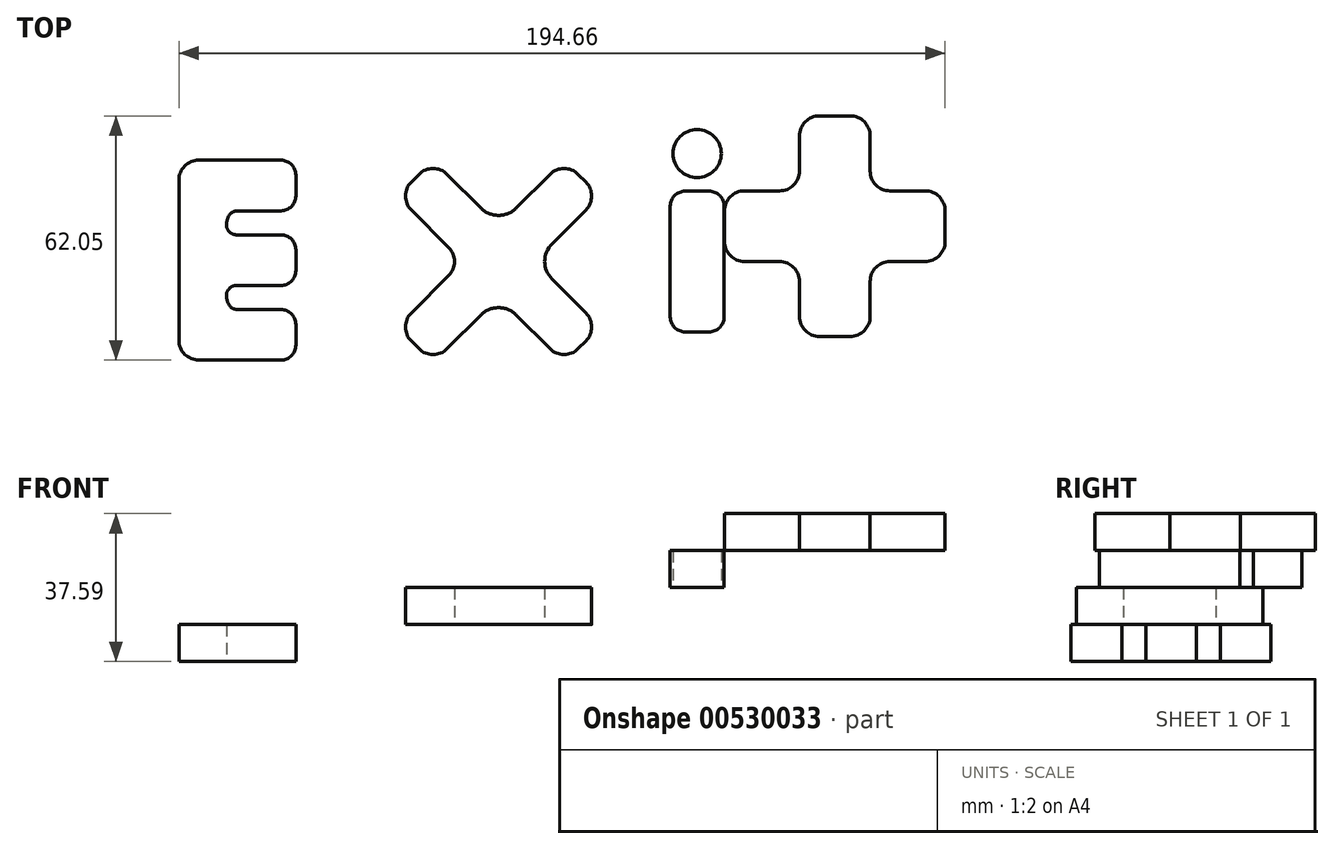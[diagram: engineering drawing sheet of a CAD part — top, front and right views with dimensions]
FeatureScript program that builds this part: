
annotation { "Feature Type Name" : "Feature", "Feature Type Description" : "" }
export const myFeature = defineFeature(function(context is Context, id is Id, definition is map)
    precondition{}
    {
        {
            var Q0;
            Q0=qCreatedBy(makeId("Top.planeOp"),FACE);
            var sketch = newSketch(context, id + "F0", { "sketchPlane" : qUnion([Q0])});
            skLineSegment(sketch, "E0", {"start": v(-56.56, 0.34) * mm, "end": v(-56.56, 20.66) * mm});
            skLineSegment(sketch, "E1", {"start": v(-56.56, 0.34) * mm, "end": v(-56.56, -19.98) * mm});
            skLineSegment(sketch, "E2", {"start": v(-51.48, 25.74) * mm, "end": v(-30.66, 25.74) * mm});
            skLineSegment(sketch, "E3", {"start": v(-26.85, 21.93) * mm, "end": v(-26.85, 16.69) * mm});
            skLineSegment(sketch, "E4", {"start": v(-30.66, 12.88) * mm, "end": v(-41.7, 12.88) * mm});
            skLineSegment(sketch, "E5", {"start": v(-51.48, -25.06) * mm, "end": v(-30.66, -25.06) * mm});
            skLineSegment(sketch, "E6", {"start": v(-26.85, -21.25) * mm, "end": v(-26.85, -16) * mm});
            skLineSegment(sketch, "E7", {"start": v(-30.66, -12.2) * mm, "end": v(-41.7, -12.2) * mm});
            skLineSegment(sketch, "E8", {"start": v(-44.4, 9.9) * mm, "end": v(-44.16, 10.93) * mm});
            skLineSegment(sketch, "E9", {"start": v(-44.4, -9.22) * mm, "end": v(-44.16, -10.24) * mm});
            skLineSegment(sketch, "E10", {"start": v(-41.94, 6.78) * mm, "end": v(-30.66, 6.78) * mm});
            skLineSegment(sketch, "E11", {"start": v(-26.85, 2.97) * mm, "end": v(-26.85, -2.28) * mm});
            skPoint(sketch, "E12.visualSharp", {"position": v(-56.56, 25.74) * mm});
            skArc(sketch, "E12.filletArc", {"start": v(-51.48, 25.74) * mm, "mid": v(-55.07, 24.26) * mm, "end": v(-56.56, 20.66) * mm});
            skPoint(sketch, "E13.visualSharp", {"position": v(-26.85, 25.74) * mm});
            skArc(sketch, "E13.filletArc", {"start": v(-26.85, 21.93) * mm, "mid": v(-27.96, 24.63) * mm, "end": v(-30.66, 25.74) * mm});
            skPoint(sketch, "E14.visualSharp", {"position": v(-56.56, -25.06) * mm});
            skArc(sketch, "E14.filletArc", {"start": v(-56.56, -19.98) * mm, "mid": v(-55.07, -23.57) * mm, "end": v(-51.48, -25.06) * mm});
            skPoint(sketch, "E15.visualSharp", {"position": v(-26.85, -25.06) * mm});
            skArc(sketch, "E15.filletArc", {"start": v(-30.66, -25.06) * mm, "mid": v(-27.96, -23.94) * mm, "end": v(-26.85, -21.25) * mm});
            skPoint(sketch, "E16.visualSharp", {"position": v(-26.85, -12.2) * mm});
            skArc(sketch, "E16.filletArc", {"start": v(-26.85, -16) * mm, "mid": v(-27.96, -13.3) * mm, "end": v(-30.66, -12.2) * mm});
            skPoint(sketch, "E17.visualSharp", {"position": v(-26.85, 12.88) * mm});
            skArc(sketch, "E17.filletArc", {"start": v(-30.66, 12.88) * mm, "mid": v(-27.96, 14) * mm, "end": v(-26.85, 16.69) * mm});
            skLineSegment(sketch, "E18", {"start": v(-30.66, -6.09) * mm, "end": v(-41.94, -6.09) * mm});
            skPoint(sketch, "E19.visualSharp", {"position": v(-26.85, 6.78) * mm});
            skArc(sketch, "E19.filletArc", {"start": v(-26.85, 2.97) * mm, "mid": v(-27.96, 5.66) * mm, "end": v(-30.66, 6.78) * mm});
            skPoint(sketch, "E20.visualSharp", {"position": v(-26.85, -6.09) * mm});
            skArc(sketch, "E20.filletArc", {"start": v(-30.66, -6.09) * mm, "mid": v(-27.96, -4.97) * mm, "end": v(-26.85, -2.28) * mm});
            skPoint(sketch, "E21.visualSharp", {"position": v(-45.15, 6.78) * mm});
            skArc(sketch, "E21.filletArc", {"start": v(-44.4, 9.9) * mm, "mid": v(-43.93, 7.74) * mm, "end": v(-41.94, 6.78) * mm});
            skPoint(sketch, "E22.visualSharp", {"position": v(-43.7, 12.88) * mm});
            skArc(sketch, "E22.filletArc", {"start": v(-41.7, 12.88) * mm, "mid": v(-43.26, 12.33) * mm, "end": v(-44.16, 10.93) * mm});
            skPoint(sketch, "E23.visualSharp", {"position": v(-45.15, -6.09) * mm});
            skArc(sketch, "E23.filletArc", {"start": v(-41.94, -6.09) * mm, "mid": v(-43.93, -7.05) * mm, "end": v(-44.4, -9.22) * mm});
            skPoint(sketch, "E24.visualSharp", {"position": v(-43.7, -12.2) * mm});
            skArc(sketch, "E24.filletArc", {"start": v(-44.16, -10.24) * mm, "mid": v(-43.26, -11.65) * mm, "end": v(-41.7, -12.2) * mm});
            skLineSegment(sketch, "E25", {"start": v(-30.66, 25.74) * mm, "end": v(20.45, 25.74) * mm});
            skLineSegment(sketch, "E26", {"start": v(-30.66, -25.06) * mm, "end": v(17.75, -25.06) * mm});
            skSolve(sketch);
        }
        {
            var Q0;
            Q0=makeQuery(id+"F0.imprint","IMPRINT",FACE,{"disambiguationData":[TD([[makeQuery(id+"F0.imprint","IMPRINT",EDGE,{"derivedFrom":sQuery(id+"F0.wireOp",EDGE,"E0")}),-1.0]])]});
            extrude(context, id + "F1", {"entities" : qUnion([Q0]), "depth" : 9.4 * mm, "offsetDistance" : 25.4 * mm});
        }
        {
            var Q0;
            Q0=makeQuery(id+"F1.opExtrude","CAP_FACE",FACE,{"disambiguationData":[OSD([sQuery(id+"F0.wireOp",EDGE,"E0"),sQuery(id+"F0.wireOp",EDGE,"E1"),sQuery(id+"F0.wireOp",EDGE,"E2"),sQuery(id+"F0.wireOp",EDGE,"E3"),sQuery(id+"F0.wireOp",EDGE,"E4"),sQuery(id+"F0.wireOp",EDGE,"E5"),sQuery(id+"F0.wireOp",EDGE,"E6"),sQuery(id+"F0.wireOp",EDGE,"E7"),sQuery(id+"F0.wireOp",EDGE,"E8"),sQuery(id+"F0.wireOp",EDGE,"E9"),sQuery(id+"F0.wireOp",EDGE,"E10"),sQuery(id+"F0.wireOp",EDGE,"E11"),sQuery(id+"F0.wireOp",EDGE,"E12.filletArc"),sQuery(id+"F0.wireOp",EDGE,"E13.filletArc"),sQuery(id+"F0.wireOp",EDGE,"E14.filletArc"),sQuery(id+"F0.wireOp",EDGE,"E15.filletArc"),sQuery(id+"F0.wireOp",EDGE,"E16.filletArc"),sQuery(id+"F0.wireOp",EDGE,"E17.filletArc"),sQuery(id+"F0.wireOp",EDGE,"E18"),sQuery(id+"F0.wireOp",EDGE,"E19.filletArc"),sQuery(id+"F0.wireOp",EDGE,"E20.filletArc"),sQuery(id+"F0.wireOp",EDGE,"E21.filletArc"),sQuery(id+"F0.wireOp",EDGE,"E22.filletArc"),sQuery(id+"F0.wireOp",EDGE,"E23.filletArc"),sQuery(id+"F0.wireOp",EDGE,"E24.filletArc")])],"isStart":false});
            var sketch = newSketch(context, id + "F2", { "sketchPlane" : qUnion([Q0])});
            skPoint(sketch, "E27.endSnap0", {"position": v(-55.07, -23.57) * mm});
            skLineSegment(sketch, "E28", {"start": v(4.41, 22.15) * mm, "end": v(2.5, 20.24) * mm});
            skLineSegment(sketch, "E29", {"start": v(2.5, 13.06) * mm, "end": v(11.96, 3.6) * mm});
            skLineSegment(sketch, "E30", {"start": v(11.6, 22.15) * mm, "end": v(20.16, 13.59) * mm});
            skLineSegment(sketch, "E31.MirrorCS", {"start": v(37.7, 22.15) * mm, "end": v(29.14, 13.59) * mm});
            skLineSegment(sketch, "E32.MirrorCS", {"start": v(46.8, 13.06) * mm, "end": v(38.24, 4.5) * mm});
            skLineSegment(sketch, "E33.MirrorCS", {"start": v(44.9, 22.15) * mm, "end": v(46.8, 20.24) * mm});
            skLineSegment(sketch, "E34.MirrorCS", {"start": v(46.8, -13.06) * mm, "end": v(38.24, -4.5) * mm});
            skLineSegment(sketch, "E35.MirrorCS", {"start": v(44.9, -22.15) * mm, "end": v(46.8, -20.24) * mm});
            skLineSegment(sketch, "E36.MirrorCS", {"start": v(37.7, -22.15) * mm, "end": v(29.14, -13.59) * mm});
            skLineSegment(sketch, "E37.MirrorCS", {"start": v(11.6, -22.15) * mm, "end": v(20.16, -13.59) * mm});
            skLineSegment(sketch, "E38.MirrorCS", {"start": v(2.5, -13.06) * mm, "end": v(11.96, -3.6) * mm});
            skLineSegment(sketch, "E39.MirrorCS", {"start": v(4.41, -22.15) * mm, "end": v(2.5, -20.24) * mm});
            skPoint(sketch, "E40.visualSharp", {"position": v(-1.1, 16.65) * mm});
            skArc(sketch, "E40.filletArc", {"start": v(2.5, 20.24) * mm, "mid": v(1.01, 16.65) * mm, "end": v(2.5, 13.06) * mm});
            skPoint(sketch, "E41.visualSharp", {"position": v(8, 25.74) * mm});
            skArc(sketch, "E41.filletArc", {"start": v(11.6, 22.15) * mm, "mid": v(8, 23.64) * mm, "end": v(4.41, 22.15) * mm});
            skPoint(sketch, "E42.visualSharp", {"position": v(-1.1, -16.65) * mm});
            skArc(sketch, "E42.filletArc", {"start": v(2.5, -13.06) * mm, "mid": v(1.01, -16.65) * mm, "end": v(2.5, -20.24) * mm});
            skPoint(sketch, "E43.visualSharp", {"position": v(8, -25.74) * mm});
            skArc(sketch, "E43.filletArc", {"start": v(4.41, -22.15) * mm, "mid": v(8, -23.64) * mm, "end": v(11.6, -22.15) * mm});
            skPoint(sketch, "E44.visualSharp", {"position": v(41.3, -25.74) * mm});
            skArc(sketch, "E44.filletArc", {"start": v(37.7, -22.15) * mm, "mid": v(41.3, -23.64) * mm, "end": v(44.9, -22.15) * mm});
            skPoint(sketch, "E45.visualSharp", {"position": v(50.4, -16.65) * mm});
            skArc(sketch, "E45.filletArc", {"start": v(46.8, -20.24) * mm, "mid": v(48.3, -16.65) * mm, "end": v(46.8, -13.06) * mm});
            skPoint(sketch, "E46.visualSharp", {"position": v(50.4, 16.65) * mm});
            skArc(sketch, "E46.filletArc", {"start": v(46.8, 13.06) * mm, "mid": v(48.3, 16.65) * mm, "end": v(46.8, 20.24) * mm});
            skPoint(sketch, "E47.visualSharp", {"position": v(41.3, 25.74) * mm});
            skArc(sketch, "E47.filletArc", {"start": v(44.9, 22.15) * mm, "mid": v(41.3, 23.64) * mm, "end": v(37.7, 22.15) * mm});
            skPoint(sketch, "E48.visualSharp", {"position": v(15.56, 0) * mm});
            skArc(sketch, "E48.filletArc", {"start": v(11.96, -3.6) * mm, "mid": v(13.45, 0) * mm, "end": v(11.96, 3.6) * mm});
            skPoint(sketch, "E49.visualSharp", {"position": v(24.65, 9.1) * mm});
            skArc(sketch, "E49.filletArc", {"start": v(20.16, 13.59) * mm, "mid": v(24.65, 11.73) * mm, "end": v(29.14, 13.59) * mm});
            skPoint(sketch, "E50.visualSharp", {"position": v(33.75, 0) * mm});
            skArc(sketch, "E50.filletArc", {"start": v(38.24, 4.5) * mm, "mid": v(36.38, 0) * mm, "end": v(38.24, -4.5) * mm});
            skPoint(sketch, "E51.visualSharp", {"position": v(24.65, -9.1) * mm});
            skArc(sketch, "E51.filletArc", {"start": v(29.14, -13.59) * mm, "mid": v(24.65, -11.73) * mm, "end": v(20.16, -13.59) * mm});
            skSolve(sketch);
        }
        {
            var Q0;
            Q0=makeQuery(id+"F2.imprint","IMPRINT",FACE,{"disambiguationData":[TD([[makeQuery(id+"F2.imprint","IMPRINT",EDGE,{"derivedFrom":sQuery(id+"F2.wireOp",EDGE,"E28")}),1.0]])]});
            extrude(context, id + "F3", {"entities" : qUnion([Q0]), "depth" : 9.4 * mm, "offsetDistance" : 25.4 * mm});
        }
        {
            var Q0;
            Q0=makeQuery(id+"F3.opExtrude","CAP_FACE",FACE,{"disambiguationData":[OSD([sQuery(id+"F2.wireOp",EDGE,"E28"),sQuery(id+"F2.wireOp",EDGE,"E29"),sQuery(id+"F2.wireOp",EDGE,"E30"),sQuery(id+"F2.wireOp",EDGE,"E31.MirrorCS"),sQuery(id+"F2.wireOp",EDGE,"E32.MirrorCS"),sQuery(id+"F2.wireOp",EDGE,"E33.MirrorCS"),sQuery(id+"F2.wireOp",EDGE,"E34.MirrorCS"),sQuery(id+"F2.wireOp",EDGE,"E35.MirrorCS"),sQuery(id+"F2.wireOp",EDGE,"E36.MirrorCS"),sQuery(id+"F2.wireOp",EDGE,"E37.MirrorCS"),sQuery(id+"F2.wireOp",EDGE,"E38.MirrorCS"),sQuery(id+"F2.wireOp",EDGE,"E39.MirrorCS"),sQuery(id+"F2.wireOp",EDGE,"E40.filletArc"),sQuery(id+"F2.wireOp",EDGE,"E41.filletArc"),sQuery(id+"F2.wireOp",EDGE,"E42.filletArc"),sQuery(id+"F2.wireOp",EDGE,"E43.filletArc"),sQuery(id+"F2.wireOp",EDGE,"E44.filletArc"),sQuery(id+"F2.wireOp",EDGE,"E45.filletArc"),sQuery(id+"F2.wireOp",EDGE,"E46.filletArc"),sQuery(id+"F2.wireOp",EDGE,"E47.filletArc"),sQuery(id+"F2.wireOp",EDGE,"E48.filletArc"),sQuery(id+"F2.wireOp",EDGE,"E49.filletArc"),sQuery(id+"F2.wireOp",EDGE,"E50.filletArc"),sQuery(id+"F2.wireOp",EDGE,"E51.filletArc")])],"isStart":false});
            var sketch = newSketch(context, id + "F4", { "sketchPlane" : qUnion([Q0])});
            skLineSegment(sketch, "E52.bottom", {"start": v(72.07, 17.87) * mm, "end": v(78.16, 17.87) * mm});
            skLineSegment(sketch, "E52.top", {"start": v(72.07, -17.87) * mm, "end": v(78.16, -17.87) * mm});
            skLineSegment(sketch, "E52.left", {"start": v(68.26, 14.06) * mm, "end": v(68.26, -14.06) * mm});
            skLineSegment(sketch, "E52.right", {"start": v(81.97, 14.06) * mm, "end": v(81.97, -14.06) * mm});
            skPoint(sketch, "E52.middle", {"position": v(75.11, 0) * mm});
            skPoint(sketch, "E52.cornerSnap0", {"position": v(33.43, 17.87) * mm});
            skCircle(sketch, "E53", {"center": v(75.11, 27.4) * mm, "radius": 6.11 * mm});
            skPoint(sketch, "E53.centerSnap0", {"position": v(75.11, 17.87) * mm});
            skPoint(sketch, "E54.visualSharp", {"position": v(68.26, 17.87) * mm});
            skArc(sketch, "E54.filletArc", {"start": v(72.07, 17.87) * mm, "mid": v(69.38, 16.75) * mm, "end": v(68.26, 14.06) * mm});
            skPoint(sketch, "E55.visualSharp", {"position": v(81.97, 17.87) * mm});
            skArc(sketch, "E55.filletArc", {"start": v(81.97, 14.06) * mm, "mid": v(80.85, 16.75) * mm, "end": v(78.16, 17.87) * mm});
            skPoint(sketch, "E56.visualSharp", {"position": v(68.26, -17.87) * mm});
            skArc(sketch, "E56.filletArc", {"start": v(68.26, -14.06) * mm, "mid": v(69.38, -16.75) * mm, "end": v(72.07, -17.87) * mm});
            skPoint(sketch, "E57.visualSharp", {"position": v(81.97, -17.87) * mm});
            skArc(sketch, "E57.filletArc", {"start": v(78.16, -17.87) * mm, "mid": v(80.85, -16.75) * mm, "end": v(81.97, -14.06) * mm});
            skSolve(sketch);
        }
        {
            var Q0;
            Q0=makeQuery(id+"F4.imprint","IMPRINT",FACE,{"disambiguationData":[TD([[makeQuery(id+"F4.imprint","IMPRINT",EDGE,{"derivedFrom":sQuery(id+"F4.wireOp",EDGE,"E52.bottom")}),-1.0]])]});
            extrude(context, id + "F5", {"entities" : qUnion([Q0]), "depth" : 9.4 * mm, "offsetDistance" : 25.4 * mm});
        }
        {
            var Q0;
            Q0=makeQuery(id+"F4.imprint","IMPRINT",FACE,{"disambiguationData":[TD([[makeQuery(id+"F4.imprint","IMPRINT",EDGE,{"derivedFrom":sQuery(id+"F4.wireOp",EDGE,"E53")}),1.0]])]});
            extrude(context, id + "F6", {"entities" : qUnion([Q0]), "depth" : 9.4 * mm, "offsetDistance" : 25.4 * mm});
        }
        {
            var Q0;
            Q0=makeQuery(id+"F6.opExtrude","CAP_FACE",FACE,{"disambiguationData":[OSD([sQuery(id+"F4.wireOp",EDGE,"E53")])],"isStart":false});
            var sketch = newSketch(context, id + "F7", { "sketchPlane" : qUnion([Q0])});
            skLineSegment(sketch, "E58", {"start": v(101.1, 31.91) * mm, "end": v(101.1, 23.02) * mm});
            skLineSegment(sketch, "E59", {"start": v(106.18, 37) * mm, "end": v(113.97, 37) * mm});
            skLineSegment(sketch, "E60", {"start": v(119.05, 31.91) * mm, "end": v(119.05, 23.02) * mm});
            skLineSegment(sketch, "E61.MirrorCS", {"start": v(119.05, -13.97) * mm, "end": v(119.05, -5.08) * mm});
            skLineSegment(sketch, "E62.MirrorCS", {"start": v(101.1, -13.97) * mm, "end": v(101.1, -5.08) * mm});
            skLineSegment(sketch, "E63.MirrorCS", {"start": v(106.18, -19.05) * mm, "end": v(113.97, -19.05) * mm});
            skLineSegment(sketch, "E64.MirrorCS", {"start": v(87.13, 0) * mm, "end": v(96.02, 0) * mm});
            skLineSegment(sketch, "E65.MirrorCS", {"start": v(87.13, 17.94) * mm, "end": v(96.02, 17.94) * mm});
            skLineSegment(sketch, "E66.MirrorCS", {"start": v(82.05, 12.86) * mm, "end": v(82.05, 5.08) * mm});
            skLineSegment(sketch, "E67.MirrorCS", {"start": v(138.1, 12.86) * mm, "end": v(138.1, 5.08) * mm});
            skLineSegment(sketch, "E68.MirrorCS", {"start": v(133.02, 17.94) * mm, "end": v(124.13, 17.94) * mm});
            skLineSegment(sketch, "E69.MirrorCS", {"start": v(133.02, 0) * mm, "end": v(124.13, 0) * mm});
            skPoint(sketch, "E70.visualSharp", {"position": v(101.1, 37) * mm});
            skArc(sketch, "E70.filletArc", {"start": v(106.18, 37) * mm, "mid": v(102.6, 35.5) * mm, "end": v(101.1, 31.91) * mm});
            skPoint(sketch, "E71.visualSharp", {"position": v(119.05, 37) * mm});
            skArc(sketch, "E71.filletArc", {"start": v(119.05, 31.91) * mm, "mid": v(117.56, 35.5) * mm, "end": v(113.97, 37) * mm});
            skPoint(sketch, "E72.visualSharp", {"position": v(82.05, 17.94) * mm});
            skArc(sketch, "E72.filletArc", {"start": v(87.13, 17.94) * mm, "mid": v(83.54, 16.46) * mm, "end": v(82.05, 12.86) * mm});
            skPoint(sketch, "E73.visualSharp", {"position": v(82.05, 0) * mm});
            skArc(sketch, "E73.filletArc", {"start": v(82.05, 5.08) * mm, "mid": v(83.54, 1.49) * mm, "end": v(87.13, 0) * mm});
            skPoint(sketch, "E74.visualSharp", {"position": v(101.1, -19.05) * mm});
            skArc(sketch, "E74.filletArc", {"start": v(101.1, -13.97) * mm, "mid": v(102.6, -17.56) * mm, "end": v(106.18, -19.05) * mm});
            skPoint(sketch, "E75.visualSharp", {"position": v(119.05, -19.05) * mm});
            skArc(sketch, "E75.filletArc", {"start": v(113.97, -19.05) * mm, "mid": v(117.56, -17.56) * mm, "end": v(119.05, -13.97) * mm});
            skPoint(sketch, "E76.visualSharp", {"position": v(138.1, 0) * mm});
            skArc(sketch, "E76.filletArc", {"start": v(133.02, 0) * mm, "mid": v(136.6, 1.49) * mm, "end": v(138.1, 5.08) * mm});
            skPoint(sketch, "E77.visualSharp", {"position": v(138.1, 17.94) * mm});
            skArc(sketch, "E77.filletArc", {"start": v(138.1, 12.86) * mm, "mid": v(136.6, 16.46) * mm, "end": v(133.02, 17.94) * mm});
            skPoint(sketch, "E78.visualSharp", {"position": v(101.1, 17.94) * mm});
            skArc(sketch, "E78.filletArc", {"start": v(96.02, 17.94) * mm, "mid": v(99.62, 19.43) * mm, "end": v(101.1, 23.02) * mm});
            skPoint(sketch, "E79.visualSharp", {"position": v(119.05, 17.94) * mm});
            skArc(sketch, "E79.filletArc", {"start": v(119.05, 23.02) * mm, "mid": v(120.54, 19.43) * mm, "end": v(124.13, 17.94) * mm});
            skPoint(sketch, "E80.visualSharp", {"position": v(101.1, 0) * mm});
            skArc(sketch, "E80.filletArc", {"start": v(101.1, -5.08) * mm, "mid": v(99.62, -1.49) * mm, "end": v(96.02, 0) * mm});
            skPoint(sketch, "E81.visualSharp", {"position": v(119.05, 0) * mm});
            skArc(sketch, "E81.filletArc", {"start": v(124.13, 0) * mm, "mid": v(120.54, -1.49) * mm, "end": v(119.05, -5.08) * mm});
            skSolve(sketch);
        }
        {
            var Q0;
            Q0=makeQuery(id+"F7.imprint","IMPRINT",FACE,{"disambiguationData":[TD([[makeQuery(id+"F7.imprint","IMPRINT",EDGE,{"derivedFrom":sQuery(id+"F7.wireOp",EDGE,"E58")}),1.0]])]});
            extrude(context, id + "F8", {"entities" : qUnion([Q0]), "depth" : 9.4 * mm, "offsetDistance" : 25.4 * mm});
        }
    });
